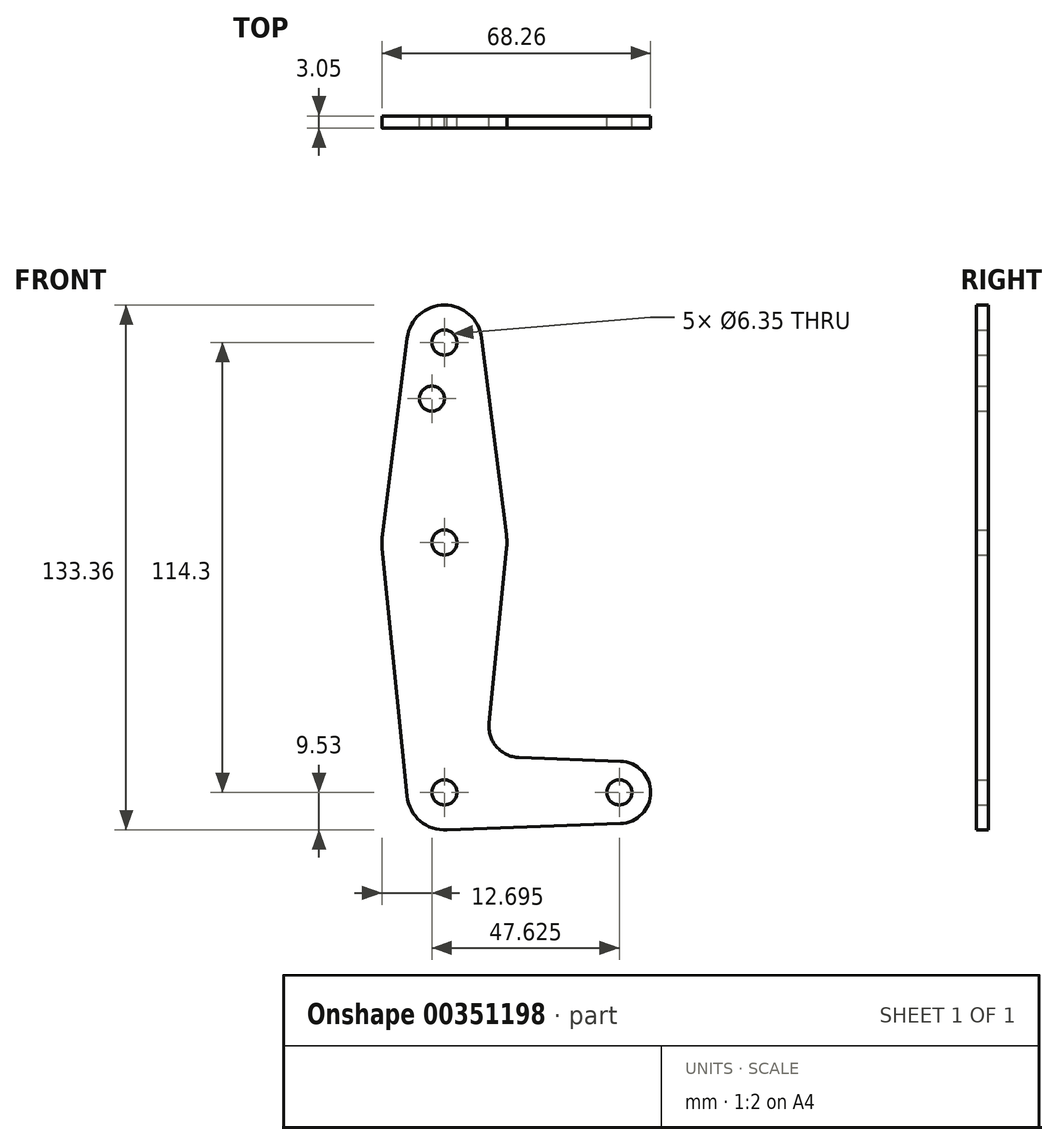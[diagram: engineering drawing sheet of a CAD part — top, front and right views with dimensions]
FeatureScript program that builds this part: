
annotation { "Feature Type Name" : "Feature", "Feature Type Description" : "" }
export const myFeature = defineFeature(function(context is Context, id is Id, definition is map)
    precondition{}
    {
        {
            var Q0;
            Q0=qCreatedBy(makeId("Front.planeOp"),FACE);
            var sketch = newSketch(context, id + "F0", { "sketchPlane" : qUnion([Q0])});
            skLineSegment(sketch, "E0", {"start": v(0, 0) * mm, "end": v(0, 114.3) * mm, "construction": true});
            skLineSegment(sketch, "E1", {"start": v(0, 0) * mm, "end": v(44.45, 0) * mm, "construction": true});
            skCircle(sketch, "E2", {"center": v(0, 0) * mm, "radius": 9.53 * mm});
            skCircle(sketch, "E3", {"center": v(44.45, 0) * mm, "radius": 7.94 * mm});
            skCircle(sketch, "E4", {"center": v(0, 114.3) * mm, "radius": 9.53 * mm});
            skCircle(sketch, "E5", {"center": v(0, 63.5) * mm, "radius": 15.88 * mm});
            skLineSegment(sketch, "E6", {"start": v(-9.45, 115.5) * mm, "end": v(-15.75, 65.48) * mm});
            skLineSegment(sketch, "E7", {"start": v(9.45, 115.5) * mm, "end": v(15.75, 65.48) * mm});
            skCircle(sketch, "E8", {"center": v(0, 114.3) * mm, "radius": 3.18 * mm});
            skCircle(sketch, "E9", {"center": v(-3.18, 100.03) * mm, "radius": 3.18 * mm});
            skCircle(sketch, "E10", {"center": v(0, 63.5) * mm, "radius": 3.18 * mm});
            skCircle(sketch, "E11", {"center": v(0, 0) * mm, "radius": 3.18 * mm});
            skCircle(sketch, "E12", {"center": v(44.45, 0) * mm, "radius": 3.18 * mm});
            skLineSegment(sketch, "E13", {"start": v(0, -9.52) * mm, "end": v(44.78, -7.93) * mm});
            skLineSegment(sketch, "E14", {"start": v(18.97, 8.85) * mm, "end": v(44.78, 7.93) * mm});
            skLineSegment(sketch, "E15", {"start": v(15.8, 61.91) * mm, "end": v(11.34, 17.6) * mm});
            skLineSegment(sketch, "E16", {"start": v(-15.8, 61.91) * mm, "end": v(-9.48, -0.95) * mm});
            skArc(sketch, "E17.filletArc", {"start": v(11.34, 17.6) * mm, "mid": v(13.26, 11.57) * mm, "end": v(18.97, 8.85) * mm});
            skSolve(sketch);
        }
        {
            var Q0;
            Q0 = qSketchRegion(id + "F0", true);
            extrude(context, id + "F1", {"entities" : qUnion([Q0]), "depth" : 3.05 * mm});
        }
    });
